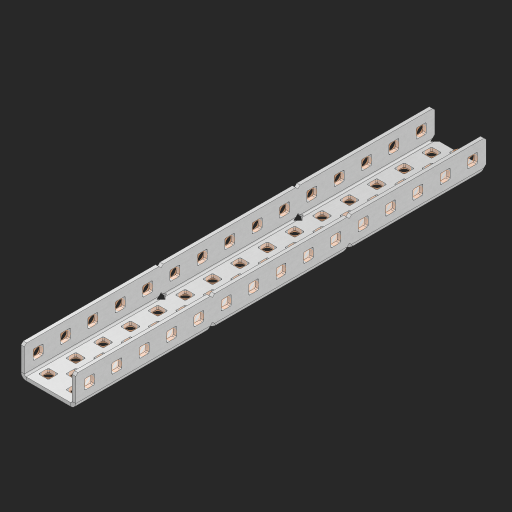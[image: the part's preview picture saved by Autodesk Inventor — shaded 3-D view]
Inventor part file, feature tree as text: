
AUTODESK INVENTOR PART (.ipt)
format: ipt  version: 2023 (Build 270158000, 158)  size: 1,174,016 bytes
history: native  units: in
note: dims shown in document units (in); Inventor stores cm internally (conversion verified against a paired STEP export)
features: other x82, extrude x73, sheet_metal_op x11, sketch x10, pattern_linear x2, mirror x1, chamfer x1
ambient origin geometry x8: Origin, YZ Plane, XZ Plane, XY Plane, X Axis, Y Axis, Z Axis, Center Point
bodies: Solid1 (feature_tree), Body (feature_tree)
feature tree (180):
  sheet_metal_op  "Flanges"
  other  "Flange Pattern Plane"
  other  "Flange Pattern Sketch"
  sheet_metal_op  "Flange Pattern"
  sheet_metal_op  "Body Pattern"
  pattern_linear  "Center Pattern"  Spacing1=0.0625in  [1 undecoded]
  other  "Arc Length"
  mirror  "Notch Mirror"
  pattern_linear  "Notch Pattern"  Spacing1=0.182in  [1 undecoded]
  chamfer  "End Chamfer"
  extrude  "Half Cut"  Depth=0.02in
  sketch  "Sketch1"  dims[d0=1.0in]
  other  "Plate1"
  sketch  "Sketch2"  dims[d1=7.5in]
  other  "Plate2"
  sheet_metal_op  "Bend1"
  sheet_metal_op  "Corner1"
  sketch  "Sketch3"  dims[d2=0.0625in]
  sketch  "Sketch7"  dims[d3=0.0625in]
  other  "Srf1"
  other  "Srf2"
  sketch  "Sketch8"  dims[d4=0.0312in]
  sketch  "Sketch9"  dims[d5=0.125in]
  other  "Srf91"
  sheet_metal_op  "Body Pattern Sketch"
  other  "Srf92"
  sketch  "Sketch13"  dims[d6=0.0625in]
  sketch  "Sketch14"  dims[d7=0.5in d8=90.0deg d9=0.0312in]
  sketch  "Sketch15"  dims[d10=0.25in]
  sketch  "Sketch16"  dims[d11=0.0625in d12=0.0625in d16=0.182in d17=0.02in d18=0.0625in d19=0.0in d20=0.25in d21=0.25in d38=5.9055in d40=0.5in d41=0.7874in d43=1.0in d46=0.172in d47=1.0in d48=0.0in d49=0.182in d50=0.02in d51=0.25in d52=0.25in d53=0.0625in d54=0.0in d55=0.172in d56=1.0in d57=0.0in d58=0.25in d60=5.9055in d62=0.5in d63=0.7874in d65=0.5in d85=0.1473in d86=0.1782in d88=0.04in d89=0.0625in d90=0.0in d91=0.04in d92=0.0491in d95=2.5in d96=0.04in d97=0.25in d98=45.0deg d99=0.25in d100=0.5in d101=0.0in d102=2.497in d106=0.182in d107=0.02in d108=0.5in d109=0.5in d110=0.0625in d111=0.0in d112=0.172in d113=0.5in d114=0.0in d117=0.5in d118=0.5in d119=0.5in]
  other  "Srf786"
  other  "Srf823"
  other  "Srf824"
  other  "Srf825"
  other  "Srf826"
  other  "Srf827"
  other  "Srf828"
  other  "Srf829"
  other  "Srf856"
  other  "Srf857"
  other  "Srf858"
  other  "Srf859"
  other  "Srf860"
  other  "Srf861"
  other  "Srf862"
  other  "Srf889"
  other  "Srf890"
  other  "Srf891"
  other  "Srf892"
  other  "Srf893"
  other  "Srf894"
  other  "Srf895"
  other  "Srf896"
  other  "Srf922"
  other  "Srf923"
  other  "Srf924"
  other  "Srf925"
  other  "Srf926"
  other  "Srf959"
  other  "Srf960"
  other  "Srf961"
  other  "Srf962"
  other  "Srf963"
  other  "Srf996"
  other  "Srf997"
  other  "Srf998"
  other  "Srf999"
  other  "Srf1000"
  other  "Srf1143"
  other  "Srf1144"
  other  "Srf1145"
  other  "Srf1146"
  other  "Srf1147"
  other  "Srf1148"
  other  "Srf1149"
  other  "Srf1150"
  other  "Srf1151"
  other  "Srf1152"
  other  "Srf1153"
  other  "Srf1154"
  other  "Srf1155"
  other  "Srf1156"
  other  "Srf1157"
  other  "Srf1158"
  other  "Srf1199"
  other  "Srf1200"
  other  "Srf1201"
  other  "Srf1202"
  other  "Srf1203"
  other  "Srf1204"
  other  "Srf1205"
  other  "Srf1206"
  other  "Srf1207"
  other  "Srf1208"
  other  "Srf1209"
  other  "Srf1210"
  other  "Srf1211"
  other  "Srf1212"
  other  "Srf1213"
  other  "Srf1214"
  other  "Srf1255"
  sheet_metal_op  "Flange Stamp"
  sheet_metal_op  "Flange Circle"
  sheet_metal_op  "Body Stamp"
  sheet_metal_op  "Body Circle"
  other  "Center Stamp"
  other  "Center Circle"
  sheet_metal_op  "Notch"
  extrude  "ExtrusionSrf2"  Depth=0.0625in
  extrude  "ExtrusionSrf92"  TaperAngle=0.0deg  [1 undecoded]
  extrude  "ExtrusionSrf823"  Depth=0.5in
  extrude  "ExtrusionSrf824"  Depth=0.5in
  extrude  "ExtrusionSrf825"  Depth=0.5in
  extrude  "ExtrusionSrf826"  Depth=0.5in
  extrude  "ExtrusionSrf827"  Depth=1.0in TaperAngle=0.0deg
  extrude  "ExtrusionSrf828"  Depth=0.5in
  extrude  "ExtrusionSrf829"  Depth=0.02in
  extrude  "ExtrusionSrf856"  Depth=0.5in
  extrude  "ExtrusionSrf857"  Depth=0.5in
  extrude  "ExtrusionSrf858"  Depth=0.0625in
  extrude  "ExtrusionSrf859"  TaperAngle=0.0deg  [1 undecoded]
  extrude  "ExtrusionSrf860"  Depth=0.5in
  extrude  "ExtrusionSrf861"  Depth=1.0in TaperAngle=0.0deg
  extrude  "ExtrusionSrf862"  Depth=0.5in
  extrude  "ExtrusionSrf889"  Depth=0.5in
  extrude  "ExtrusionSrf890"  Depth=0.5in
  extrude  "ExtrusionSrf891"  Depth=0.5in
  extrude  "ExtrusionSrf892"  Depth=0.5in
  extrude  "ExtrusionSrf893"  Depth=0.5in
  extrude  "ExtrusionSrf894"  Depth=0.0625in
  extrude  "ExtrusionSrf895"  TaperAngle=0.0deg  [1 undecoded]
  extrude  "ExtrusionSrf896"  Depth=0.5in
  extrude  "ExtrusionSrf922"  Depth=0.5in
  extrude  "ExtrusionSrf923"  Depth=2.5in
  extrude  "ExtrusionSrf924"  Depth=0.5in TaperAngle=45.0deg
  extrude  "ExtrusionSrf925"  Depth=0.5in
  extrude  "ExtrusionSrf926"  Depth=0.5in TaperAngle=0.0deg
  extrude  "ExtrusionSrf959"  Depth=0.5in
  extrude  "ExtrusionSrf960"  Depth=0.5in
  extrude  "ExtrusionSrf961"  Depth=0.02in
  extrude  "ExtrusionSrf962"  Depth=0.5in
  extrude  "ExtrusionSrf963"  Depth=0.5in
  extrude  "ExtrusionSrf996"  Depth=0.0625in
  extrude  "ExtrusionSrf997"  TaperAngle=0.0deg  [1 undecoded]
  extrude  "ExtrusionSrf998"  Depth=0.5in
  extrude  "ExtrusionSrf999"  Depth=0.5in TaperAngle=0.0deg
  extrude  "ExtrusionSrf1000"  Depth=0.5in
  extrude  "ExtrusionSrf1143"  Depth=0.5in
  extrude  "ExtrusionSrf1144"  Depth=0.5in
  extrude  "ExtrusionSrf1145"  [1 undecoded]
  extrude  "ExtrusionSrf1146"  [1 undecoded]
  extrude  "ExtrusionSrf1147"  [1 undecoded]
  extrude  "ExtrusionSrf1148"  [1 undecoded]
  extrude  "ExtrusionSrf1149"  [1 undecoded]
  extrude  "ExtrusionSrf1150"  [1 undecoded]
  extrude  "ExtrusionSrf1151"  [1 undecoded]
  extrude  "ExtrusionSrf1152"  [1 undecoded]
  extrude  "ExtrusionSrf1153"  [1 undecoded]
  extrude  "ExtrusionSrf1154"  [1 undecoded]
  extrude  "ExtrusionSrf1155"  [1 undecoded]
  extrude  "ExtrusionSrf1156"  [1 undecoded]
  extrude  "ExtrusionSrf1157"  [1 undecoded]
  extrude  "ExtrusionSrf1158"  [1 undecoded]
  extrude  "ExtrusionSrf1199"  [1 undecoded]
  extrude  "ExtrusionSrf1200"  [1 undecoded]
  extrude  "ExtrusionSrf1201"  [1 undecoded]
  extrude  "ExtrusionSrf1202"  [1 undecoded]
  extrude  "ExtrusionSrf1203"  [1 undecoded]
  extrude  "ExtrusionSrf1204"  [1 undecoded]
  extrude  "ExtrusionSrf1205"  [1 undecoded]
  extrude  "ExtrusionSrf1206"  [1 undecoded]
  extrude  "ExtrusionSrf1207"  [1 undecoded]
  extrude  "ExtrusionSrf1208"  [1 undecoded]
  extrude  "ExtrusionSrf1209"  [1 undecoded]
  extrude  "ExtrusionSrf1210"  [1 undecoded]
  extrude  "ExtrusionSrf1211"  [1 undecoded]
  extrude  "ExtrusionSrf1212"  [1 undecoded]
  extrude  "ExtrusionSrf1213"  [1 undecoded]
  extrude  "ExtrusionSrf1214"  [1 undecoded]
  extrude  "ExtrusionSrf1255"  [1 undecoded]
note: 37 required parameter values undecoded (feature->parameter linkage not recoverable at this tier; creation-order binding heuristic only, values carry confidence <= 0.55)
